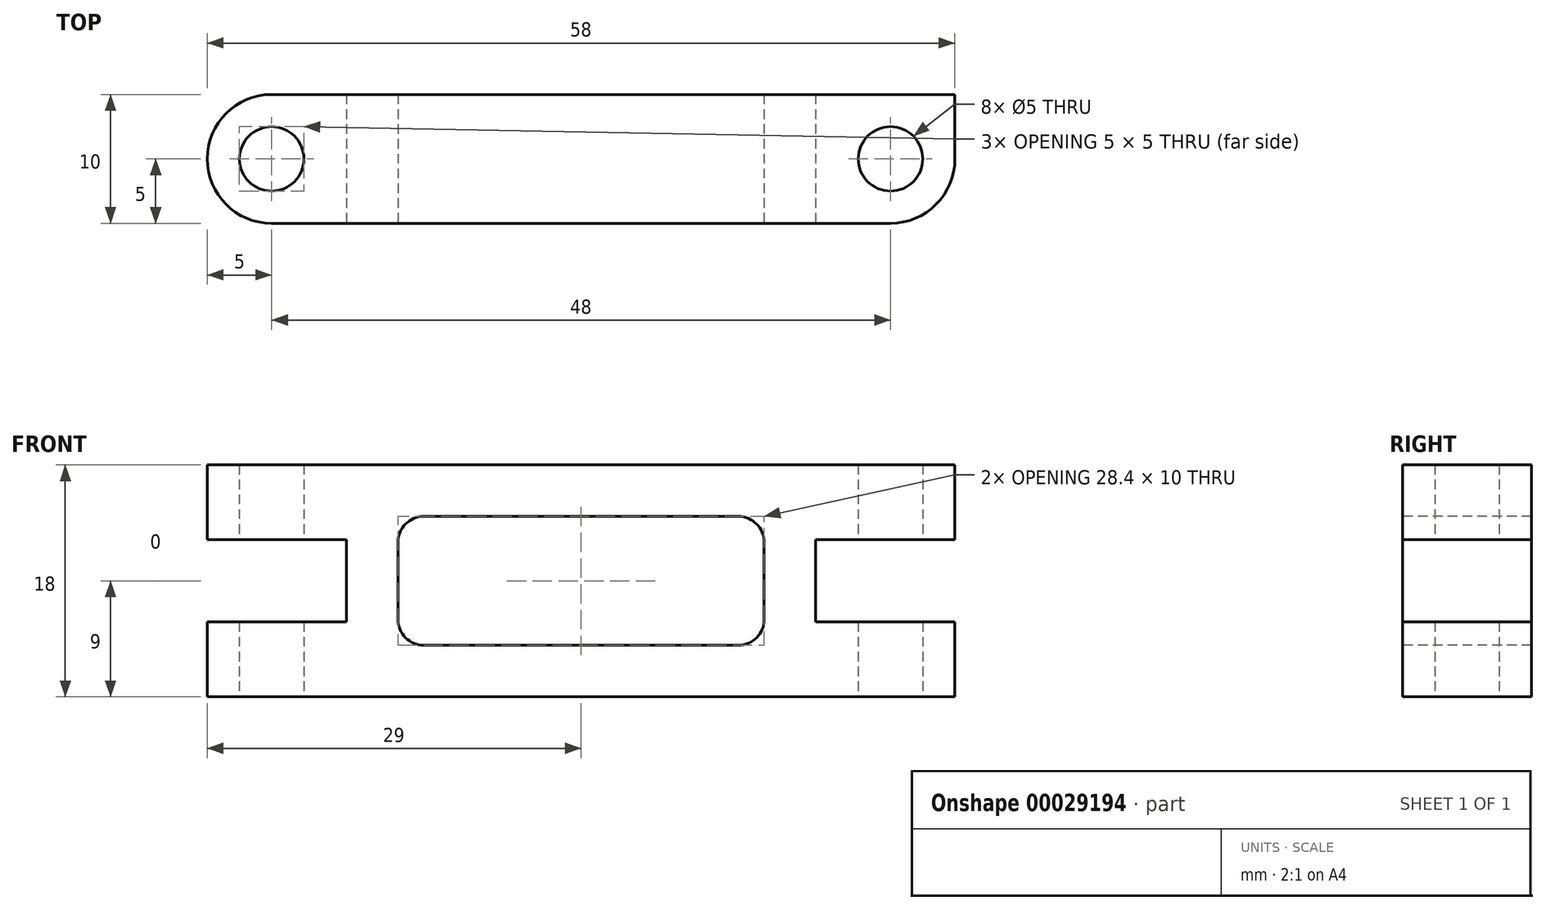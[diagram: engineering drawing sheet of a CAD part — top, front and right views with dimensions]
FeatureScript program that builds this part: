
annotation { "Feature Type Name" : "Feature", "Feature Type Description" : "" }
export const myFeature = defineFeature(function(context is Context, id is Id, definition is map)
    precondition{}
    {
        {
            var Q0;
            Q0=qCreatedBy(makeId("Top.planeOp"),FACE);
            var sketch = newSketch(context, id + "F0", { "sketchPlane" : qUnion([Q0])});
            skLineSegment(sketch, "E0.bottom", {"start": v(5, 0) * mm, "end": v(53, 0) * mm});
            skLineSegment(sketch, "E0.top", {"start": v(5, 10) * mm, "end": v(58, 10) * mm});
            skLineSegment(sketch, "E0.left", {"start": v(0, 5) * mm, "end": v(0, 5) * mm});
            skLineSegment(sketch, "E0.right", {"start": v(58, 5) * mm, "end": v(58, 10) * mm});
            skLineSegment(sketch, "E1", {"start": v(-7.04, 5) * mm, "end": v(80.33, 5) * mm, "construction": true});
            skCircle(sketch, "E2", {"center": v(5, 5) * mm, "radius": 2.5 * mm});
            skCircle(sketch, "E3", {"center": v(53, 5) * mm, "radius": 2.5 * mm});
            skPoint(sketch, "E4.visualSharp", {"position": v(0, 10) * mm});
            skArc(sketch, "E4.filletArc", {"start": v(5, 10) * mm, "mid": v(1.46, 8.54) * mm, "end": v(0, 5) * mm});
            skPoint(sketch, "E5.visualSharp", {"position": v(0, 0) * mm});
            skArc(sketch, "E5.filletArc", {"start": v(0, 5) * mm, "mid": v(1.46, 1.46) * mm, "end": v(5, 0) * mm});
            skPoint(sketch, "E6.visualSharp", {"position": v(58, 0) * mm});
            skArc(sketch, "E6.filletArc", {"start": v(53, 0) * mm, "mid": v(56.54, 1.46) * mm, "end": v(58, 5) * mm});
            skLineSegment(sketch, "E7", {"start": v(10, 10) * mm, "end": v(10, 0) * mm});
            skLineSegment(sketch, "E8", {"start": v(48, 10) * mm, "end": v(48, 0) * mm});
            skSolve(sketch);
        }
        {
            var Q0;
            Q0=makeQuery(id+"F0.imprint","IMPRINT",FACE,{"disambiguationData":[TD([[makeQuery(id+"F0.imprint","IMPRINT",EDGE,{"derivedFrom":sQuery(id+"F0.wireOp",EDGE,"E2")}),-1.0]])]});
            var Q1;
            {var subQ1=sQuery(id+"F0.wireOp",EDGE,"E7");Q1=makeQuery(id+"F0.imprint","IMPRINT",FACE,{"disambiguationData":[TD([[makeQuery(id+"F0.imprint","IMPRINT",EDGE,{"derivedFrom":subQ1}),1.0]])]});}
            var Q2;
            {var subQ2=sQuery(id+"F0.wireOp",EDGE,"E0.right");Q2=makeQuery(id+"F0.imprint","IMPRINT",FACE,{"disambiguationData":[TD([[makeQuery(id+"F0.imprint","IMPRINT",EDGE,{"derivedFrom":subQ2}),1.0]])]});}
            extrude(context, id + "F1", {"entities" : qUnion([Q0, Q1, Q2]), "depth" : 18 * mm});
        }
        {
            var Q0;
            Q0=qCreatedBy(makeId("Front.planeOp"),FACE);
            var sketch = newSketch(context, id + "F2", { "sketchPlane" : qUnion([Q0])});
            skLineSegment(sketch, "E9", {"start": v(0, 5.8) * mm, "end": v(10.8, 5.8) * mm});
            skLineSegment(sketch, "E10", {"start": v(10.8, 5.8) * mm, "end": v(10.8, 12.2) * mm});
            skLineSegment(sketch, "E11", {"start": v(10.8, 12.2) * mm, "end": v(0, 12.2) * mm});
            skLineSegment(sketch, "E12", {"start": v(0, 5.8) * mm, "end": v(0, 12.2) * mm});
            skLineSegment(sketch, "E13.bottom", {"start": v(0, 0) * mm, "end": v(58, 0) * mm});
            skLineSegment(sketch, "E13.top", {"start": v(0, 18) * mm, "end": v(58, 18) * mm});
            skLineSegment(sketch, "E13.left", {"start": v(0, 0) * mm, "end": v(0, 18) * mm});
            skLineSegment(sketch, "E13.right", {"start": v(58, 0) * mm, "end": v(58, 18) * mm});
            skLineSegment(sketch, "E14.bottom", {"start": v(47.2, 12.2) * mm, "end": v(58, 12.2) * mm});
            skLineSegment(sketch, "E14.top", {"start": v(47.2, 5.8) * mm, "end": v(58, 5.8) * mm});
            skLineSegment(sketch, "E14.left", {"start": v(47.2, 12.2) * mm, "end": v(47.2, 5.8) * mm});
            skLineSegment(sketch, "E14.right", {"start": v(58, 12.2) * mm, "end": v(58, 5.8) * mm});
            skLineSegment(sketch, "E15", {"start": v(14.8, 12) * mm, "end": v(14.8, 6) * mm});
            skLineSegment(sketch, "E16", {"start": v(16.8, 4) * mm, "end": v(41.2, 4) * mm});
            skLineSegment(sketch, "E17", {"start": v(43.2, 6) * mm, "end": v(43.2, 12) * mm});
            skLineSegment(sketch, "E18", {"start": v(41.2, 14) * mm, "end": v(16.8, 14) * mm});
            skPoint(sketch, "E19.visualSharp", {"position": v(14.8, 14) * mm});
            skArc(sketch, "E19.filletArc", {"start": v(16.8, 14) * mm, "mid": v(15.39, 13.41) * mm, "end": v(14.8, 12) * mm});
            skPoint(sketch, "E20.visualSharp", {"position": v(14.8, 4) * mm});
            skArc(sketch, "E20.filletArc", {"start": v(14.8, 6) * mm, "mid": v(15.39, 4.59) * mm, "end": v(16.8, 4) * mm});
            skPoint(sketch, "E21.visualSharp", {"position": v(43.2, 4) * mm});
            skArc(sketch, "E21.filletArc", {"start": v(41.2, 4) * mm, "mid": v(42.61, 4.59) * mm, "end": v(43.2, 6) * mm});
            skPoint(sketch, "E22.visualSharp", {"position": v(43.2, 14) * mm});
            skArc(sketch, "E22.filletArc", {"start": v(43.2, 12) * mm, "mid": v(42.61, 13.41) * mm, "end": v(41.2, 14) * mm});
            skSolve(sketch);
        }
        {
            var Q0;
            {var subQ2=sQuery(id+"F2.wireOp",EDGE,"E9");Q0=makeQuery(id+"F2.imprint","IMPRINT",FACE,{"disambiguationData":[TD([[makeQuery(id+"F2.imprint","IMPRINT",EDGE,{"derivedFrom":subQ2}),1.0]])]});}
            var Q1;
            Q1=makeQuery(id+"F2.imprint","IMPRINT",FACE,{"disambiguationData":[TD([[makeQuery(id+"F2.imprint","IMPRINT",EDGE,{"derivedFrom":sQuery(id+"F2.wireOp",EDGE,"E15")}),1.0]])]});
            var Q2;
            Q2=makeQuery(id+"F2.imprint","IMPRINT",FACE,{"disambiguationData":[TD([[makeQuery(id+"F2.imprint","IMPRINT",EDGE,{"derivedFrom":sQuery(id+"F2.wireOp",EDGE,"E14.bottom")}),-1.0]])]});
            extrude(context, id + "F3", {"entities" : qUnion([Q0, Q1, Q2]), "operationType" : NewBodyOperationType.REMOVE, "endBound" : BoundingType.THROUGH_ALL, "oppositeDirection" : true, "depth" : 25 * mm});
        }
    });
